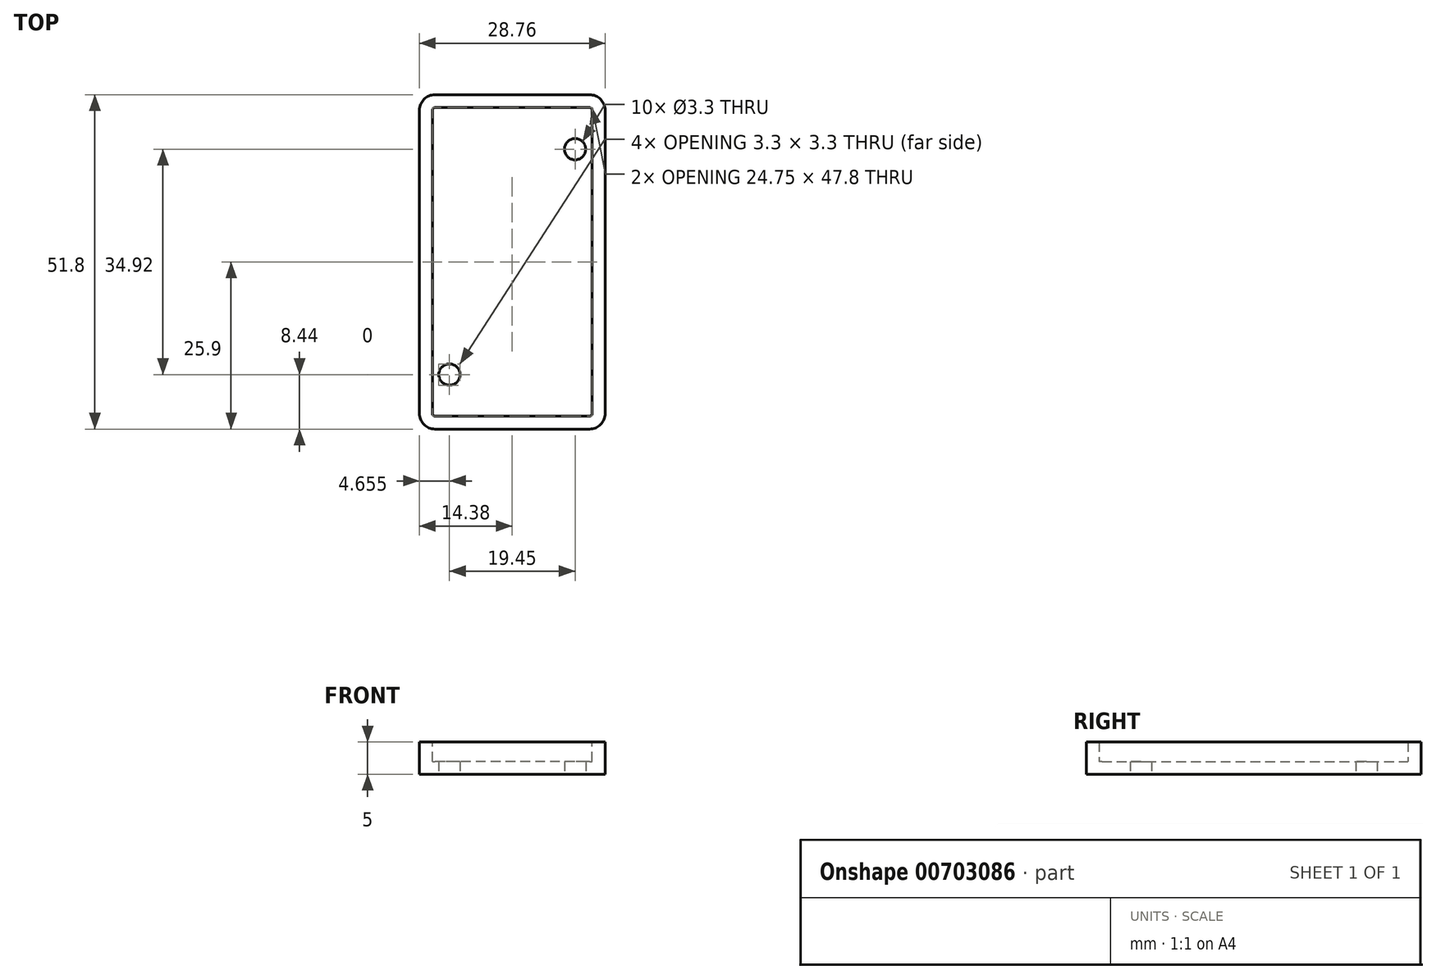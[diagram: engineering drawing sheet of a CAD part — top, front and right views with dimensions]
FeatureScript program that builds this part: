
annotation { "Feature Type Name" : "Feature", "Feature Type Description" : "" }
export const myFeature = defineFeature(function(context is Context, id is Id, definition is map)
    precondition{}
    {
        {
            var Q0;
            Q0=qCreatedBy(makeId("Top.planeOp"),FACE);
            var sketch = newSketch(context, id + "F0", { "sketchPlane" : qUnion([Q0])});
            skLineSegment(sketch, "E0.bottom", {"start": v(14.38, -25.9) * mm, "end": v(-14.37, -25.9) * mm});
            skLineSegment(sketch, "E0.top", {"start": v(14.37, 25.9) * mm, "end": v(-14.38, 25.9) * mm});
            skLineSegment(sketch, "E0.left", {"start": v(14.38, -25.9) * mm, "end": v(14.37, 25.9) * mm});
            skLineSegment(sketch, "E0.right", {"start": v(-14.37, -25.9) * mm, "end": v(-14.38, 25.9) * mm});
            skPoint(sketch, "E0.middle", {"position": v(0, 0) * mm});
            skPoint(sketch, "E1", {"position": v(9.72, 17.46) * mm});
            skPoint(sketch, "E2", {"position": v(-9.72, -17.46) * mm});
            skSolve(sketch);
        }
        {
            var Q0;
            Q0=makeQuery(id+"F0.imprint","IMPRINT",FACE,{"disambiguationData":[TD([[makeQuery(id+"F0.imprint","IMPRINT",EDGE,{"derivedFrom":sQuery(id+"F0.wireOp",EDGE,"E0.bottom")}),-1.0]])]});
            extrude(context, id + "F1", {"entities" : qUnion([Q0]), "depth" : 5 * mm, "offsetDistance" : 25 * mm});
        }
        {
            var Q0;
            Q0=makeQuery(id+"F1.opExtrude","SWEPT_EDGE",EDGE,{"disambiguationData":[OSD([sQuery(id+"F0.wireOp",EDGE,"E0.bottom"),sQuery(id+"F0.wireOp",EDGE,"E0.left")])]});
            var Q1;
            Q1=makeQuery(id+"F1.opExtrude","SWEPT_EDGE",EDGE,{"disambiguationData":[OSD([sQuery(id+"F0.wireOp",EDGE,"E0.bottom"),sQuery(id+"F0.wireOp",EDGE,"E0.right")])]});
            var Q2;
            Q2=makeQuery(id+"F1.opExtrude","SWEPT_EDGE",EDGE,{"disambiguationData":[OSD([sQuery(id+"F0.wireOp",EDGE,"E0.top"),sQuery(id+"F0.wireOp",EDGE,"E0.left")])]});
            var Q3;
            Q3=makeQuery(id+"F1.opExtrude","SWEPT_EDGE",EDGE,{"disambiguationData":[OSD([sQuery(id+"F0.wireOp",EDGE,"E0.top"),sQuery(id+"F0.wireOp",EDGE,"E0.right")])]});
            fillet(context, id + "F2", {"entities" : qUnion([Q0, Q1, Q2, Q3]), "radius" : 2.41 * mm, "tangentPropagation" : true, "allowEdgeOverflow" : false});
        }
        {
            var Q0;
            Q0=makeQuery(id+"F1.opExtrude","CAP_FACE",FACE,{"disambiguationData":[OSD([sQuery(id+"F0.wireOp",EDGE,"E0.bottom"),sQuery(id+"F0.wireOp",EDGE,"E0.top"),sQuery(id+"F0.wireOp",EDGE,"E0.left"),sQuery(id+"F0.wireOp",EDGE,"E0.right")])],"isStart":false});
            shell(context, id + "F3", {"entities" : qUnion([Q0]), "thickness" : 2 * mm});
        }
        {
            var Q0;
            Q0=sQuery(id+"F0.wireOp",VERTEX,"E1");
            var Q1;
            Q1=sQuery(id+"F0.wireOp",VERTEX,"E2");
            var Q2;
            Q2=makeQuery(id+"F1.opExtrude","SWEPT_BODY",BODY,{"disambiguationData":[OSD([sQuery(id+"F0.wireOp",EDGE,"E0.bottom"),sQuery(id+"F0.wireOp",EDGE,"E0.top"),sQuery(id+"F0.wireOp",EDGE,"E0.left"),sQuery(id+"F0.wireOp",EDGE,"E0.right")])]});
            hole(context, id + "F4", {"style" : HoleStyle.SIMPLE, "endStyle" : HoleEndStyle.THROUGH, "oppositeDirection" : true, "standardTappedOrClearance" : lookupTablePath({ "standard" : "ISO", "fit" : "Normal", "size" : "M3", "type" : "Clearance" }), "standardBlindInLast" : lookupTablePath({ "fit" : "Standard", "standard" : "ISO", "size" : "M3", "type" : "Clearance" }), "holeDiameter" : 3.3 * mm, "majorDiameter" : 5 * mm, "isTappedThrough" : true, "tappedDepth" : 12 * mm, "tapClearance" : 3, "locations" : qUnion([Q0, Q1]), "scope" : qUnion([Q2])});
        }
    });
